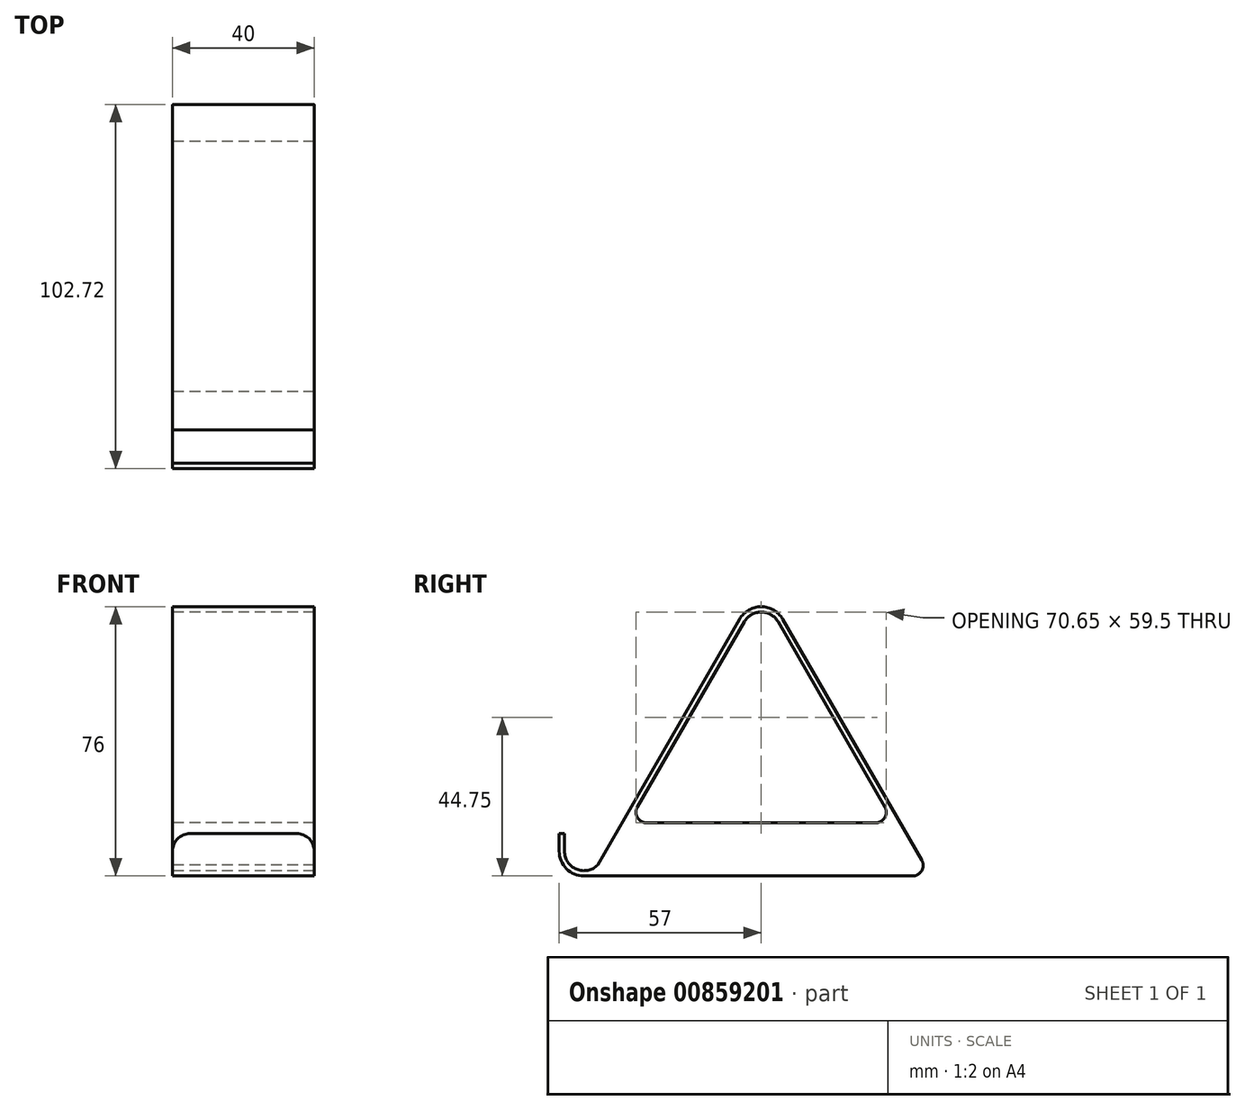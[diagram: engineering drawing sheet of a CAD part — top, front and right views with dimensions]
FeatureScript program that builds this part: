
annotation { "Feature Type Name" : "Feature", "Feature Type Description" : "" }
export const myFeature = defineFeature(function(context is Context, id is Id, definition is map)
    precondition{}
    {
        {
            var Q0;
            Q0=qCreatedBy(makeId("Right.planeOp"),FACE);
            var sketch = newSketch(context, id + "F0", { "sketchPlane" : qUnion([Q0])});
            skArc(sketch, "E0", {"start": v(-7, 0) * mm, "mid": v(-4.95, -4.95) * mm, "end": v(0, -7) * mm});
            skArc(sketch, "E1", {"start": v(54.76, 64.75) * mm, "mid": v(50, 67.5) * mm, "end": v(45.24, 64.75) * mm});
            skLineSegment(sketch, "E2", {"start": v(15.08, 12.5) * mm, "end": v(45.24, 64.75) * mm});
            skLineSegment(sketch, "E3", {"start": v(50, 62) * mm, "end": v(50, -47.48) * mm, "construction": true});
            skLineSegment(sketch, "E4", {"start": v(0, -7) * mm, "end": v(92.72, -7) * mm, "construction": true});
            skPoint(sketch, "E5.orphan", {"position": v(94.92, -4.82) * mm});
            skLineSegment(sketch, "E6", {"start": v(-7, 0) * mm, "end": v(-7, 5) * mm});
            skLineSegment(sketch, "E7.0", {"start": v(-5.5, 0) * mm, "end": v(-5.5, 5) * mm});
            skLineSegment(sketch, "E7.1", {"start": v(95.32, -2.5) * mm, "end": v(56.06, 65.5) * mm});
            skArc(sketch, "E7.2", {"start": v(56.06, 65.5) * mm, "mid": v(50, 69) * mm, "end": v(43.94, 65.5) * mm});
            skLineSegment(sketch, "E7.3", {"start": v(3.87, -3.9) * mm, "end": v(43.94, 65.5) * mm});
            skArc(sketch, "E7.4", {"start": v(-5.5, 0) * mm, "mid": v(-2.11, -5.08) * mm, "end": v(3.87, -3.9) * mm});
            skLineSegment(sketch, "E8", {"start": v(-7, 5) * mm, "end": v(-5.5, 5) * mm});
            skLineSegment(sketch, "E9", {"start": v(0, -7) * mm, "end": v(97.91, -7) * mm});
            skLineSegment(sketch, "E10.0", {"start": v(17.67, 8) * mm, "end": v(82.33, 8) * mm});
            skPoint(sketch, "E11.orphan", {"position": v(5.08, -4.82) * mm});
            skLineSegment(sketch, "E12.trimOffspring", {"start": v(84.92, 12.5) * mm, "end": v(54.76, 64.75) * mm});
            skPoint(sketch, "E13.visualSharp", {"position": v(12.48, 8) * mm});
            skArc(sketch, "E13.filletArc", {"start": v(15.08, 12.5) * mm, "mid": v(15.08, 9.5) * mm, "end": v(17.67, 8) * mm});
            skPoint(sketch, "E14.visualSharp", {"position": v(87.52, 8) * mm});
            skArc(sketch, "E14.filletArc", {"start": v(82.33, 8) * mm, "mid": v(84.92, 9.5) * mm, "end": v(84.92, 12.5) * mm});
            skArc(sketch, "E15.filletArc", {"start": v(92.72, -7) * mm, "mid": v(95.32, -5.5) * mm, "end": v(95.32, -2.5) * mm});
            skSolve(sketch);
        }
        {
            var Q0;
            Q0 = qSketchRegion(id + "F0", true);
            extrude(context, id + "F1", {"entities" : qUnion([Q0]), "depth" : 40 * mm, "offsetDistance" : 25 * mm});
        }
        {
            var Q0;
            Q0=makeQuery(id+"F1.opExtrude","CAP_EDGE",EDGE,{"disambiguationData":[OSD([sQuery(id+"F0.wireOp",EDGE,"E8")])],"isStart":false});
            var Q1;
            Q1=makeQuery(id+"F1.opExtrude","CAP_EDGE",EDGE,{"disambiguationData":[OSD([sQuery(id+"F0.wireOp",EDGE,"E8")])],"isStart":true});
            fillet(context, id + "F2", {"entities" : qUnion([Q0, Q1]), "radius" : 5 * mm, "tangentPropagation" : true, "allowEdgeOverflow" : false});
        }
    });
